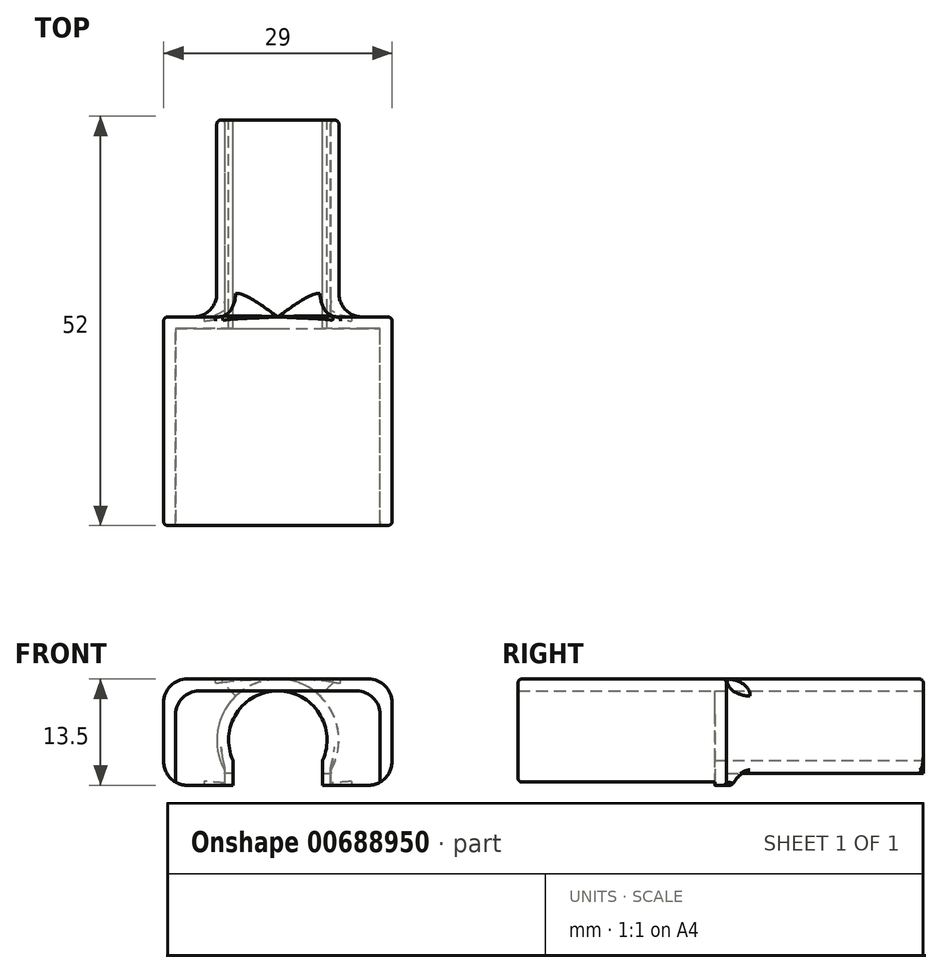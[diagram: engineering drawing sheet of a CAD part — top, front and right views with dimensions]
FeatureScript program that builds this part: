
annotation { "Feature Type Name" : "Feature", "Feature Type Description" : "" }
export const myFeature = defineFeature(function(context is Context, id is Id, definition is map)
    precondition{}
    {
        {
            var Q0;
            Q0=qCreatedBy(makeId("Front.planeOp"),FACE);
            var sketch = newSketch(context, id + "F0", { "sketchPlane" : qUnion([Q0])});
            skLineSegment(sketch, "E0.bottom", {"start": v(0, 0) * mm, "end": v(26, 0) * mm});
            skLineSegment(sketch, "E0.top", {"start": v(0, -12) * mm, "end": v(26, -12) * mm});
            skLineSegment(sketch, "E0.left", {"start": v(0, 0) * mm, "end": v(0, -12) * mm});
            skLineSegment(sketch, "E0.right", {"start": v(26, 0) * mm, "end": v(26, -12) * mm});
            skLineSegment(sketch, "E1.top", {"start": v(0, 1.5) * mm, "end": v(26, 1.5) * mm});
            skLineSegment(sketch, "E1.left", {"start": v(0, 0) * mm, "end": v(0, 1.5) * mm});
            skLineSegment(sketch, "E1.right", {"start": v(26, 0) * mm, "end": v(26, 1.5) * mm});
            skLineSegment(sketch, "E2.bottom", {"start": v(26, 1.5) * mm, "end": v(27.5, 1.5) * mm});
            skLineSegment(sketch, "E2.top", {"start": v(26, -12) * mm, "end": v(27.5, -12) * mm});
            skLineSegment(sketch, "E2.left", {"start": v(26, 1.5) * mm, "end": v(26, -12) * mm});
            skLineSegment(sketch, "E2.right", {"start": v(27.5, 1.5) * mm, "end": v(27.5, -12) * mm});
            skLineSegment(sketch, "E3.bottom", {"start": v(0, 1.5) * mm, "end": v(-1.5, 1.5) * mm});
            skLineSegment(sketch, "E3.top", {"start": v(0, -12) * mm, "end": v(-1.5, -12) * mm});
            skLineSegment(sketch, "E3.left", {"start": v(0, 1.5) * mm, "end": v(0, -12) * mm});
            skLineSegment(sketch, "E3.right", {"start": v(-1.5, 1.5) * mm, "end": v(-1.5, -12) * mm});
            skLineSegment(sketch, "E4.bottom", {"start": v(0, -12) * mm, "end": v(2, -12) * mm});
            skLineSegment(sketch, "E4.top", {"start": v(0, -11) * mm, "end": v(2, -11) * mm});
            skLineSegment(sketch, "E4.left", {"start": v(0, -12) * mm, "end": v(0, -11) * mm});
            skLineSegment(sketch, "E4.right", {"start": v(2, -12) * mm, "end": v(2, -11) * mm});
            skLineSegment(sketch, "E5.bottom", {"start": v(26, -12) * mm, "end": v(24, -12) * mm});
            skLineSegment(sketch, "E5.top", {"start": v(26, -11) * mm, "end": v(24, -11) * mm});
            skLineSegment(sketch, "E5.left", {"start": v(26, -12) * mm, "end": v(26, -11) * mm});
            skLineSegment(sketch, "E5.right", {"start": v(24, -12) * mm, "end": v(24, -11) * mm});
            skLineSegment(sketch, "E6.top", {"start": v(0, -10.5) * mm, "end": v(2, -10.5) * mm});
            skLineSegment(sketch, "E6.left", {"start": v(0, -11) * mm, "end": v(0, -10.5) * mm});
            skLineSegment(sketch, "E6.right", {"start": v(2, -11) * mm, "end": v(2, -10.5) * mm});
            skLineSegment(sketch, "E7.top", {"start": v(26, -10.5) * mm, "end": v(24, -10.5) * mm});
            skLineSegment(sketch, "E7.left", {"start": v(26, -11) * mm, "end": v(26, -10.5) * mm});
            skLineSegment(sketch, "E7.right", {"start": v(24, -11) * mm, "end": v(24, -10.5) * mm});
            skSolve(sketch);
        }
        {
            var Q0;
            Q0=makeQuery(id+"F0.imprint","IMPRINT",FACE,{"disambiguationData":[TD([[makeQuery(id+"F0.imprint","IMPRINT",EDGE,{"derivedFrom":sQuery(id+"F0.wireOp",EDGE,"E4.bottom")}),1.0]])]});
            var Q1;
            Q1=makeQuery(id+"F0.imprint","IMPRINT",FACE,{"disambiguationData":[TD([[makeQuery(id+"F0.imprint","IMPRINT",EDGE,{"derivedFrom":sQuery(id+"F0.wireOp",EDGE,"E5.bottom")}),-1.0]])]});
            var Q2;
            {var subQ0=sQuery(id+"F0.wireOp",EDGE,"E0.bottom");Q2=makeQuery(id+"F0.imprint","IMPRINT",FACE,{"disambiguationData":[TD([[makeQuery(id+"F0.imprint","IMPRINT",EDGE,{"derivedFrom":subQ0}),1.0]])]});}
            var Q3;
            {var subQ3=sQuery(id+"F0.wireOp",EDGE,"E2.bottom");Q3=makeQuery(id+"F0.imprint","IMPRINT",FACE,{"disambiguationData":[TD([[makeQuery(id+"F0.imprint","IMPRINT",EDGE,{"derivedFrom":subQ3}),-1.0]])]});}
            var Q4;
            {var subQ3=sQuery(id+"F0.wireOp",EDGE,"E3.bottom");Q4=makeQuery(id+"F0.imprint","IMPRINT",FACE,{"disambiguationData":[TD([[makeQuery(id+"F0.imprint","IMPRINT",EDGE,{"derivedFrom":subQ3}),1.0]])]});}
            extrude(context, id + "F1", {"entities" : qUnion([Q0, Q1, Q2, Q3, Q4]), "depth" : 25 * mm, "offsetDistance" : 25 * mm});
        }
        {
            var Q0;
            Q0=makeQuery(id+"F1.opExtrude","CAP_FACE",FACE,{"disambiguationData":[OSD([sQuery(id+"F0.wireOp",EDGE,"E0.bottom"),sQuery(id+"F0.wireOp",EDGE,"E1.top"),sQuery(id+"F0.wireOp",EDGE,"E2.bottom"),sQuery(id+"F0.wireOp",EDGE,"E2.top"),sQuery(id+"F0.wireOp",EDGE,"E2.left"),sQuery(id+"F0.wireOp",EDGE,"E2.right"),sQuery(id+"F0.wireOp",EDGE,"E3.bottom"),sQuery(id+"F0.wireOp",EDGE,"E3.top"),sQuery(id+"F0.wireOp",EDGE,"E3.left"),sQuery(id+"F0.wireOp",EDGE,"E3.right"),sQuery(id+"F0.wireOp",EDGE,"E4.bottom"),sQuery(id+"F0.wireOp",EDGE,"E4.right"),sQuery(id+"F0.wireOp",EDGE,"E5.bottom"),sQuery(id+"F0.wireOp",EDGE,"E5.right"),sQuery(id+"F0.wireOp",EDGE,"E4.top"),sQuery(id+"F0.wireOp",EDGE,"E6.left"),sQuery(id+"F0.wireOp",EDGE,"E5.top"),sQuery(id+"F0.wireOp",EDGE,"E7.left")])],"isStart":true});
            var sketch = newSketch(context, id + "F2", { "sketchPlane" : qUnion([Q0])});
            skLineSegment(sketch, "E8.bottom", {"start": v(-27.5, 1.5) * mm, "end": v(1.5, 1.5) * mm});
            skLineSegment(sketch, "E8.top", {"start": v(-27.5, -12) * mm, "end": v(1.5, -12) * mm});
            skLineSegment(sketch, "E8.left", {"start": v(-27.5, 1.5) * mm, "end": v(-27.5, -12) * mm});
            skLineSegment(sketch, "E8.right", {"start": v(1.5, 1.5) * mm, "end": v(1.5, -12) * mm});
            skSolve(sketch);
        }
        {
            var Q0;
            Q0 = qSketchRegion(id + "F2", true);
            extrude(context, id + "F3", {"entities" : qUnion([Q0]), "operationType" : NewBodyOperationType.ADD, "depth" : 1.5 * mm, "offsetDistance" : 25 * mm});
        }
        {
            var Q0;
            Q0=makeQuery(id+"F3.opExtrude","CAP_FACE",FACE,{"disambiguationData":[OSD([sQuery(id+"F2.wireOp",EDGE,"E8.bottom"),sQuery(id+"F2.wireOp",EDGE,"E8.top"),sQuery(id+"F2.wireOp",EDGE,"E8.left"),sQuery(id+"F2.wireOp",EDGE,"E8.right")])],"isStart":false});
            var sketch = newSketch(context, id + "F4", { "sketchPlane" : qUnion([Q0])});
            skLineSegment(sketch, "E9", {"start": v(-13, 1.5) * mm, "end": v(-13, -6.25) * mm, "construction": true});
            skCircle(sketch, "E10", {"center": v(-13, -6.25) * mm, "radius": 7.75 * mm});
            skCircle(sketch, "E11", {"center": v(-13, -6.25) * mm, "radius": 6.25 * mm});
            skLineSegment(sketch, "E12", {"start": v(-18.2, -12) * mm, "end": v(-18.2, -9.72) * mm});
            skLineSegment(sketch, "E13", {"start": v(-7.8, -12) * mm, "end": v(-7.8, -9.72) * mm});
            skLineSegment(sketch, "E14", {"start": v(-7.8, -12) * mm, "end": v(-7.3, -12) * mm, "construction": true});
            skLineSegment(sketch, "E15", {"start": v(-18.2, -12) * mm, "end": v(-18.7, -12) * mm, "construction": true});
            skLineSegment(sketch, "E16", {"start": v(-7.3, -12) * mm, "end": v(-7.3, -8.82) * mm});
            skLineSegment(sketch, "E17", {"start": v(-18.7, -12) * mm, "end": v(-18.7, -8.82) * mm});
            skLineSegment(sketch, "E18", {"start": v(-7.3, -12) * mm, "end": v(-6.3, -12) * mm, "construction": true});
            skLineSegment(sketch, "E19", {"start": v(-18.7, -12) * mm, "end": v(-19.7, -12) * mm, "construction": true});
            skLineSegment(sketch, "E20", {"start": v(-19.7, -12) * mm, "end": v(-19.7, -10.15) * mm});
            skLineSegment(sketch, "E21", {"start": v(-6.3, -12) * mm, "end": v(-6.3, -10.15) * mm});
            skSolve(sketch);
        }
        {
            var Q0;
            {var subQ1=makeQuery(id+"F3.opExtrude","CAP_EDGE",EDGE,{"disambiguationData":[OSD([sQuery(id+"F2.wireOp",EDGE,"E8.top")])],"isStart":false});var subQ4=sQuery(id+"F4.wireOp",EDGE,"E11");var subQ5=makeQuery(id+"F4.imprint","INTERSECT",VERTEX,{"disambiguationData":[OD(0.0)],"derivedFrom":[subQ1,subQ4]});Q0=makeQuery(id+"F4.imprint","IMPRINT",FACE,{"disambiguationData":[TD([[makeQuery(id+"F4.imprint","IMPRINT",EDGE,{"disambiguationData":[TD([[subQ5,-1.0]])],"derivedFrom":subQ4}),-1.0]])]});}
            var Q1;
            {var subQ0=sQuery(id+"F4.wireOp",EDGE,"E11");var subQ5=makeQuery(id+"F4.imprint","INTERSECT",VERTEX,{"derivedFrom":[subQ0,sQuery(id+"F4.wireOp",EDGE,"E12")]});Q1=makeQuery(id+"F4.imprint","IMPRINT",FACE,{"disambiguationData":[TD([[makeQuery(id+"F4.imprint","IMPRINT",EDGE,{"disambiguationData":[TD([[subQ5,1.0]])],"derivedFrom":subQ0}),1.0]])]});}
            var Q2;
            {var subQ0=sQuery(id+"F4.wireOp",EDGE,"E12");Q2=makeQuery(id+"F4.imprint","IMPRINT",FACE,{"disambiguationData":[TD([[makeQuery(id+"F4.imprint","IMPRINT",EDGE,{"derivedFrom":subQ0}),-1.0]])]});}
            var Q3;
            {var subQ0=sQuery(id+"F4.wireOp",EDGE,"E13");Q3=makeQuery(id+"F4.imprint","IMPRINT",FACE,{"disambiguationData":[TD([[makeQuery(id+"F4.imprint","IMPRINT",EDGE,{"derivedFrom":subQ0}),1.0]])]});}
            var Q4;
            {var subQ1=makeQuery(id+"F3.opExtrude","CAP_EDGE",EDGE,{"disambiguationData":[OSD([sQuery(id+"F2.wireOp",EDGE,"E8.top")])],"isStart":false});var subQ3=sQuery(id+"F4.wireOp",EDGE,"E16");var subQ5=makeQuery(id+"F4.imprint","INTERSECT",VERTEX,{"derivedFrom":[subQ1,subQ3]});Q4=makeQuery(id+"F4.imprint","IMPRINT",FACE,{"disambiguationData":[TD([[makeQuery(id+"F4.imprint","IMPRINT",EDGE,{"disambiguationData":[TD([[subQ5,-1.0]])],"derivedFrom":subQ3}),1.0]])]});}
            var Q5;
            {var subQ1=makeQuery(id+"F3.opExtrude","CAP_EDGE",EDGE,{"disambiguationData":[OSD([sQuery(id+"F2.wireOp",EDGE,"E8.top")])],"isStart":false});var subQ3=sQuery(id+"F4.wireOp",EDGE,"E17");var subQ5=makeQuery(id+"F4.imprint","INTERSECT",VERTEX,{"derivedFrom":[subQ1,subQ3]});Q5=makeQuery(id+"F4.imprint","IMPRINT",FACE,{"disambiguationData":[TD([[makeQuery(id+"F4.imprint","IMPRINT",EDGE,{"disambiguationData":[TD([[subQ5,-1.0]])],"derivedFrom":subQ3}),-1.0]])]});}
            var Q6;
            {var subQ0=sQuery(id+"F4.wireOp",EDGE,"E12");Q6=makeQuery(id+"F4.imprint","IMPRINT",FACE,{"disambiguationData":[TD([[makeQuery(id+"F4.imprint","IMPRINT",EDGE,{"derivedFrom":subQ0}),1.0]])]});}
            var Q7;
            {var subQ0=sQuery(id+"F4.wireOp",EDGE,"E13");Q7=makeQuery(id+"F4.imprint","IMPRINT",FACE,{"disambiguationData":[TD([[makeQuery(id+"F4.imprint","IMPRINT",EDGE,{"derivedFrom":subQ0}),-1.0]])]});}
            extrude(context, id + "F5", {"entities" : qUnion([Q0, Q1, Q2, Q3, Q4, Q5, Q6, Q7]), "operationType" : NewBodyOperationType.REMOVE, "oppositeDirection" : true, "depth" : 2 * mm, "offsetDistance" : 25 * mm});
        }
        {
            var Q0;
            {var subQ3=sQuery(id+"F4.wireOp",EDGE,"E10");var subQ6=sQuery(id+"F4.wireOp",EDGE,"E17");var subQ8=makeQuery(id+"F4.imprint","INTERSECT",VERTEX,{"derivedFrom":[subQ3,subQ6]});Q0=makeQuery(id+"F4.imprint","IMPRINT",FACE,{"disambiguationData":[TD([[makeQuery(id+"F4.imprint","IMPRINT",EDGE,{"disambiguationData":[TD([[subQ8,1.0]])],"derivedFrom":subQ3}),1.0]])]});}
            var Q1;
            {var subQ0=sQuery(id+"F4.wireOp",EDGE,"E21");Q1=makeQuery(id+"F4.imprint","IMPRINT",FACE,{"disambiguationData":[TD([[makeQuery(id+"F4.imprint","IMPRINT",EDGE,{"derivedFrom":subQ0}),1.0]])]});}
            var Q2;
            {var subQ0=sQuery(id+"F4.wireOp",EDGE,"E20");Q2=makeQuery(id+"F4.imprint","IMPRINT",FACE,{"disambiguationData":[TD([[makeQuery(id+"F4.imprint","IMPRINT",EDGE,{"derivedFrom":subQ0}),-1.0]])]});}
            extrude(context, id + "F6", {"entities" : qUnion([Q0, Q1, Q2]), "operationType" : NewBodyOperationType.ADD, "depth" : 25 * mm, "offsetDistance" : 25 * mm});
        }
        {
            var Q0;
            Q0=makeQuery(id+"F1.opExtrude","SWEPT_EDGE",EDGE,{"disambiguationData":[OSD([sQuery(id+"F0.wireOp",EDGE,"E5.left"),sQuery(id+"F0.wireOp",EDGE,"E5.top"),sQuery(id+"F0.wireOp",EDGE,"E7.left")])]});
            var Q1;
            Q1=makeQuery(id+"F1.opExtrude","SWEPT_EDGE",EDGE,{"disambiguationData":[OSD([sQuery(id+"F0.wireOp",EDGE,"E4.left"),sQuery(id+"F0.wireOp",EDGE,"E4.top"),sQuery(id+"F0.wireOp",EDGE,"E6.left")])]});
            var Q2;
            Q2=makeQuery(id+"F1.opExtrude","SWEPT_EDGE",EDGE,{"disambiguationData":[OSD([sQuery(id+"F0.wireOp",EDGE,"E0.bottom"),sQuery(id+"F0.wireOp",EDGE,"E3.left")])]});
            var Q3;
            Q3=makeQuery(id+"F1.opExtrude","SWEPT_EDGE",EDGE,{"disambiguationData":[OSD([sQuery(id+"F0.wireOp",EDGE,"E0.bottom"),sQuery(id+"F0.wireOp",EDGE,"E2.left")])]});
            var Q4;
            Q4=makeQuery(id+"F3.boolean.opBoolean","MERGE",EDGE,{"derivedFrom":[makeQuery(id+"F1.opExtrude","SWEPT_EDGE",EDGE,{"disambiguationData":[OSD([sQuery(id+"F0.wireOp",EDGE,"E2.bottom"),sQuery(id+"F0.wireOp",EDGE,"E2.right")])]}),makeQuery(id+"F3.opExtrude","SWEPT_EDGE",EDGE,{"disambiguationData":[OSD([sQuery(id+"F2.wireOp",EDGE,"E8.bottom"),sQuery(id+"F2.wireOp",EDGE,"E8.left")])]})]});
            var Q5;
            Q5=makeQuery(id+"F3.boolean.opBoolean","MERGE",EDGE,{"derivedFrom":[makeQuery(id+"F1.opExtrude","SWEPT_EDGE",EDGE,{"disambiguationData":[OSD([sQuery(id+"F0.wireOp",EDGE,"E2.top"),sQuery(id+"F0.wireOp",EDGE,"E2.right")])]}),makeQuery(id+"F3.opExtrude","SWEPT_EDGE",EDGE,{"disambiguationData":[OSD([sQuery(id+"F2.wireOp",EDGE,"E8.top"),sQuery(id+"F2.wireOp",EDGE,"E8.left")])]})]});
            var Q6;
            Q6=makeQuery(id+"F3.boolean.opBoolean","MERGE",EDGE,{"derivedFrom":[makeQuery(id+"F1.opExtrude","SWEPT_EDGE",EDGE,{"disambiguationData":[OSD([sQuery(id+"F0.wireOp",EDGE,"E3.bottom"),sQuery(id+"F0.wireOp",EDGE,"E3.right")])]}),makeQuery(id+"F3.opExtrude","SWEPT_EDGE",EDGE,{"disambiguationData":[OSD([sQuery(id+"F2.wireOp",EDGE,"E8.bottom"),sQuery(id+"F2.wireOp",EDGE,"E8.right")])]})]});
            var Q7;
            Q7=makeQuery(id+"F3.boolean.opBoolean","MERGE",EDGE,{"derivedFrom":[makeQuery(id+"F1.opExtrude","SWEPT_EDGE",EDGE,{"disambiguationData":[OSD([sQuery(id+"F0.wireOp",EDGE,"E3.top"),sQuery(id+"F0.wireOp",EDGE,"E3.right")])]}),makeQuery(id+"F3.opExtrude","SWEPT_EDGE",EDGE,{"disambiguationData":[OSD([sQuery(id+"F2.wireOp",EDGE,"E8.top"),sQuery(id+"F2.wireOp",EDGE,"E8.right")])]})]});
            var Q8;
            {var subQ0=sQuery(id+"F4.wireOp",EDGE,"E12");var subQ3=sQuery(id+"F4.wireOp",EDGE,"E10");Q8=makeQuery(id+"F6.boolean.opBoolean","SPLIT",EDGE,{"disambiguationData":[TD([makeQuery(id+"F5.boolean.opBoolean","COPY",FACE,{"derivedFrom":makeQuery(id+"F5.opExtrude","SWEPT_FACE",FACE,{"disambiguationData":[OSD([subQ0])]})})])],"derivedFrom":makeQuery(id+"F6.opExtrude","CAP_EDGE",EDGE,{"disambiguationData":[OSD([subQ3])],"isStart":true})});}
            fillet(context, id + "F7", {"entities" : qUnion([Q0, Q1, Q2, Q3, Q4, Q5, Q6, Q7, Q8]), "radius" : 3 * mm, "tangentPropagation" : true, "allowEdgeOverflow" : false});
        }
        {
            var Q0;
            Q0=makeQuery(id+"F1.opExtrude","SWEPT_EDGE",EDGE,{"disambiguationData":[OSD([sQuery(id+"F0.wireOp",EDGE,"E0.top"),sQuery(id+"F0.wireOp",EDGE,"E4.bottom"),sQuery(id+"F0.wireOp",EDGE,"E4.right")])]});
            var Q1;
            Q1=makeQuery(id+"F1.opExtrude","SWEPT_EDGE",EDGE,{"disambiguationData":[OSD([sQuery(id+"F0.wireOp",EDGE,"E0.top"),sQuery(id+"F0.wireOp",EDGE,"E5.bottom"),sQuery(id+"F0.wireOp",EDGE,"E5.right")])]});
            var Q2;
            Q2=makeQuery(id+"F3.opExtrude","CAP_EDGE",EDGE,{"disambiguationData":[OSD([sQuery(id+"F2.wireOp",EDGE,"E8.right")])],"isStart":false});
            var Q3;
            Q3=makeQuery(id+"F1.opExtrude","CAP_EDGE",EDGE,{"disambiguationData":[OSD([sQuery(id+"F0.wireOp",EDGE,"E1.top"),sQuery(id+"F0.wireOp",EDGE,"E2.bottom"),sQuery(id+"F0.wireOp",EDGE,"E3.bottom")])],"isStart":false});
            var Q4;
            Q4=makeQuery(id+"F6.opExtrude","CAP_EDGE",EDGE,{"disambiguationData":[OSD([sQuery(id+"F4.wireOp",EDGE,"E10")])],"isStart":false});
            fillet(context, id + "F8", {"entities" : qUnion([Q0, Q1, Q2, Q3, Q4]), "radius" : .5 * mm, "tangentPropagation" : true, "allowEdgeOverflow" : false});
        }
        {
            var Q0;
            Q0=makeQuery(id+"F6.opExtrude","CAP_FACE",FACE,{"disambiguationData":[OSD([sQuery(id+"F2.wireOp",EDGE,"E8.top"),sQuery(id+"F4.wireOp",EDGE,"E10"),sQuery(id+"F4.wireOp",EDGE,"E11"),sQuery(id+"F4.wireOp",EDGE,"E16"),sQuery(id+"F4.wireOp",EDGE,"E17"),sQuery(id+"F4.wireOp",EDGE,"E20"),sQuery(id+"F4.wireOp",EDGE,"E21")])],"isStart":false});
            var sketch = newSketch(context, id + "F9", { "sketchPlane" : qUnion([Q0])});
            skLineSegment(sketch, "E22.bottom", {"start": v(-18.7, -12) * mm, "end": v(-19.7, -12) * mm});
            skLineSegment(sketch, "E22.top", {"start": v(-18.7, -10.5) * mm, "end": v(-19.7, -10.5) * mm});
            skLineSegment(sketch, "E22.left", {"start": v(-18.7, -12) * mm, "end": v(-18.7, -10.5) * mm});
            skLineSegment(sketch, "E22.right", {"start": v(-19.7, -12) * mm, "end": v(-19.7, -10.5) * mm});
            skLineSegment(sketch, "E23.bottom", {"start": v(-7.3, -12) * mm, "end": v(-6.3, -12) * mm});
            skLineSegment(sketch, "E23.top", {"start": v(-7.3, -10.5) * mm, "end": v(-6.3, -10.5) * mm});
            skLineSegment(sketch, "E23.left", {"start": v(-7.3, -12) * mm, "end": v(-7.3, -10.5) * mm});
            skLineSegment(sketch, "E23.right", {"start": v(-6.3, -12) * mm, "end": v(-6.3, -10.5) * mm});
            skSolve(sketch);
        }
        {
            var Q0;
            Q0 = qSketchRegion(id + "F9", true);
            extrude(context, id + "F10", {"entities" : qUnion([Q0]), "operationType" : NewBodyOperationType.REMOVE, "oppositeDirection" : true, "depth" : 25 * mm, "offsetDistance" : 25 * mm});
        }
        {
            var Q0;
            Q0=makeQuery(id+"F10.boolean.opBoolean","COPY",EDGE,{"derivedFrom":makeQuery(id+"F10.opExtrude","CAP_EDGE",EDGE,{"disambiguationData":[OSD([sQuery(id+"F9.wireOp",EDGE,"E22.bottom")])],"isStart":false})});
            var Q1;
            Q1=makeQuery(id+"F10.boolean.opBoolean","COPY",EDGE,{"derivedFrom":makeQuery(id+"F10.opExtrude","CAP_EDGE",EDGE,{"disambiguationData":[OSD([sQuery(id+"F9.wireOp",EDGE,"E23.bottom")])],"isStart":false})});
            var Q2;
            Q2=makeQuery(id+"F10.boolean.opBoolean","COPY",EDGE,{"derivedFrom":makeQuery(id+"F10.opExtrude","CAP_EDGE",EDGE,{"disambiguationData":[OSD([sQuery(id+"F9.wireOp",EDGE,"E23.left")])],"isStart":false})});
            var Q3;
            Q3=makeQuery(id+"F10.boolean.opBoolean","COPY",EDGE,{"derivedFrom":makeQuery(id+"F10.opExtrude","CAP_EDGE",EDGE,{"disambiguationData":[OSD([sQuery(id+"F9.wireOp",EDGE,"E22.left")])],"isStart":false})});
            var Q4;
            Q4=makeQuery(id+"F10.boolean.opBoolean","COPY",EDGE,{"derivedFrom":makeQuery(id+"F10.opExtrude","SWEPT_EDGE",EDGE,{"disambiguationData":[OSD([sQuery(id+"F4.wireOp",EDGE,"E17"),sQuery(id+"F9.wireOp",EDGE,"E22.top"),sQuery(id+"F9.wireOp",EDGE,"E22.left")])]})});
            var Q5;
            Q5=makeQuery(id+"F10.boolean.opBoolean","COPY",EDGE,{"derivedFrom":makeQuery(id+"F10.opExtrude","SWEPT_EDGE",EDGE,{"disambiguationData":[OSD([sQuery(id+"F4.wireOp",EDGE,"E16"),sQuery(id+"F9.wireOp",EDGE,"E23.top"),sQuery(id+"F9.wireOp",EDGE,"E23.left")])]})});
            var Q6;
            Q6=makeQuery(id+"F6.opExtrude","SWEPT_EDGE",EDGE,{"disambiguationData":[OSD([sQuery(id+"F4.wireOp",EDGE,"E10"),sQuery(id+"F4.wireOp",EDGE,"E21")])]});
            var Q7;
            Q7=makeQuery(id+"F6.opExtrude","SWEPT_EDGE",EDGE,{"disambiguationData":[OSD([sQuery(id+"F4.wireOp",EDGE,"E10"),sQuery(id+"F4.wireOp",EDGE,"E20")])]});
            fillet(context, id + "F11", {"entities" : qUnion([Q0, Q1, Q2, Q3, Q4, Q5, Q6, Q7]), "radius" : .5 * mm, "tangentPropagation" : true, "allowEdgeOverflow" : false});
        }
    });
